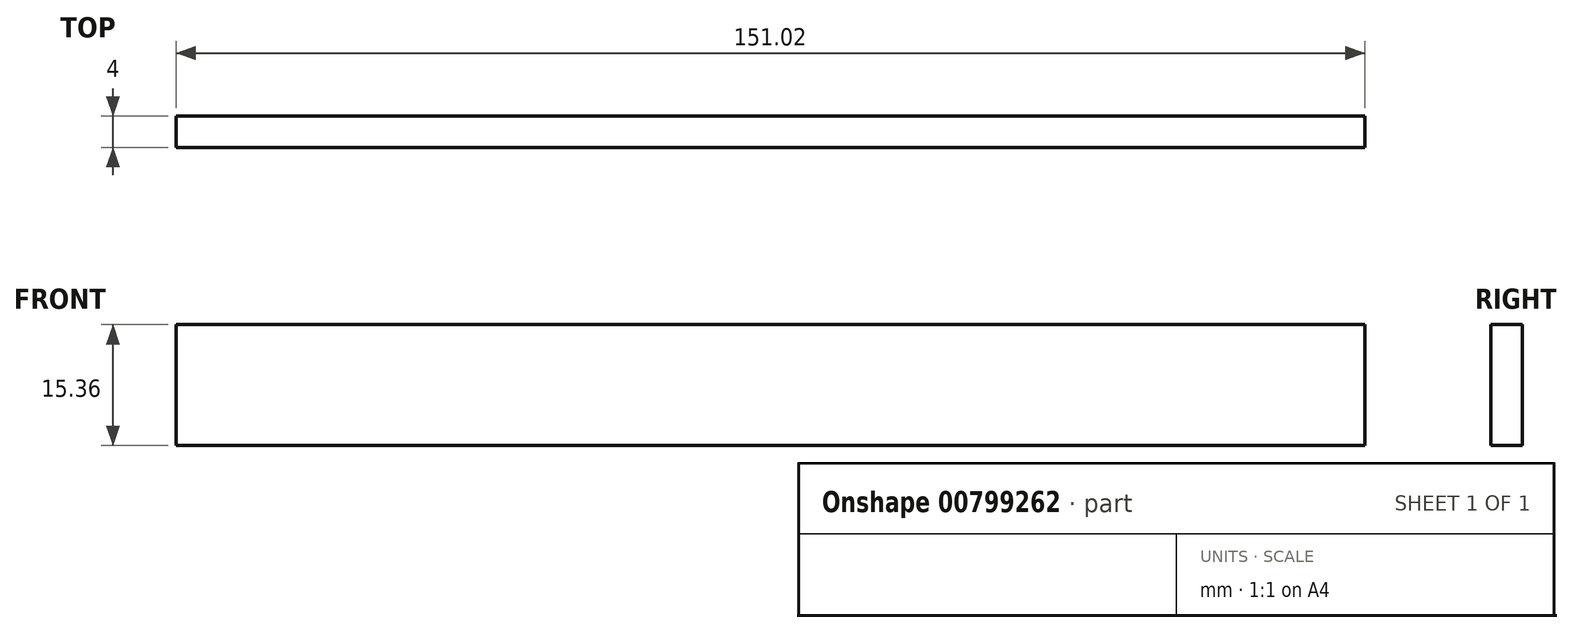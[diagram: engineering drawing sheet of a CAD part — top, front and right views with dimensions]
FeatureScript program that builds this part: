
annotation { "Feature Type Name" : "Feature", "Feature Type Description" : "" }
export const myFeature = defineFeature(function(context is Context, id is Id, definition is map)
    precondition{}
    {
        {
            var Q0;
            Q0=qCreatedBy(makeId("Front.planeOp"),FACE);
            var sketch = newSketch(context, id + "F0", { "sketchPlane" : qUnion([Q0])});
            skLineSegment(sketch, "E0.bottom", {"start": v(75.51, 7.68) * mm, "end": v(-75.51, 7.68) * mm});
            skLineSegment(sketch, "E0.top", {"start": v(75.51, -7.68) * mm, "end": v(-75.51, -7.68) * mm});
            skLineSegment(sketch, "E0.left", {"start": v(75.51, 7.68) * mm, "end": v(75.51, -7.68) * mm});
            skLineSegment(sketch, "E0.right", {"start": v(-75.51, 7.68) * mm, "end": v(-75.51, -7.68) * mm});
            skPoint(sketch, "E0.middle", {"position": v(0, 0) * mm});
            skSolve(sketch);
        }
        {
            var Q0;
            Q0 = qSketchRegion(id + "F0", true);
            extrude(context, id + "F1", {"entities" : qUnion([Q0]), "depth" : 4 * mm, "offsetDistance" : 25 * mm});
        }
    });
